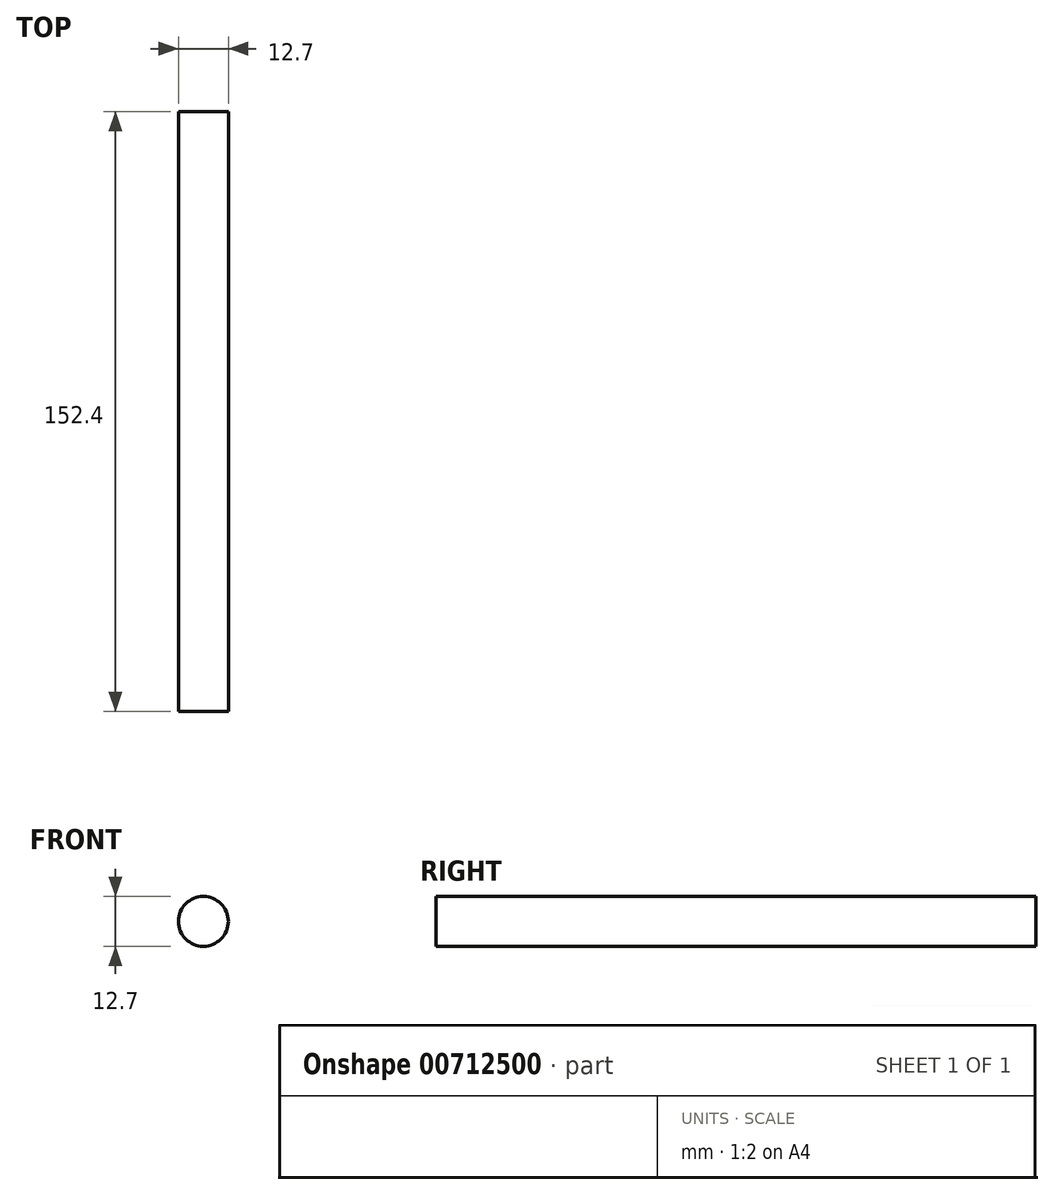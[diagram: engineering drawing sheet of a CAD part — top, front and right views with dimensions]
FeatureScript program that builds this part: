
annotation { "Feature Type Name" : "Feature", "Feature Type Description" : "" }
export const myFeature = defineFeature(function(context is Context, id is Id, definition is map)
    precondition{}
    {
        {
            var Q0;
            Q0=qCreatedBy(makeId("Front.planeOp"),FACE);
            var sketch = newSketch(context, id + "F0", { "sketchPlane" : qUnion([Q0])});
            skCircle(sketch, "E0", {"center": v(0, 0) * mm, "radius": 6.35 * mm});
            skSolve(sketch);
        }
        {
            var Q0;
            Q0 = qSketchRegion(id + "F0", true);
            extrude(context, id + "F1", {"entities" : qUnion([Q0]), "depth" : 152.4 * mm, "offsetDistance" : 25.4 * mm});
        }
    });
